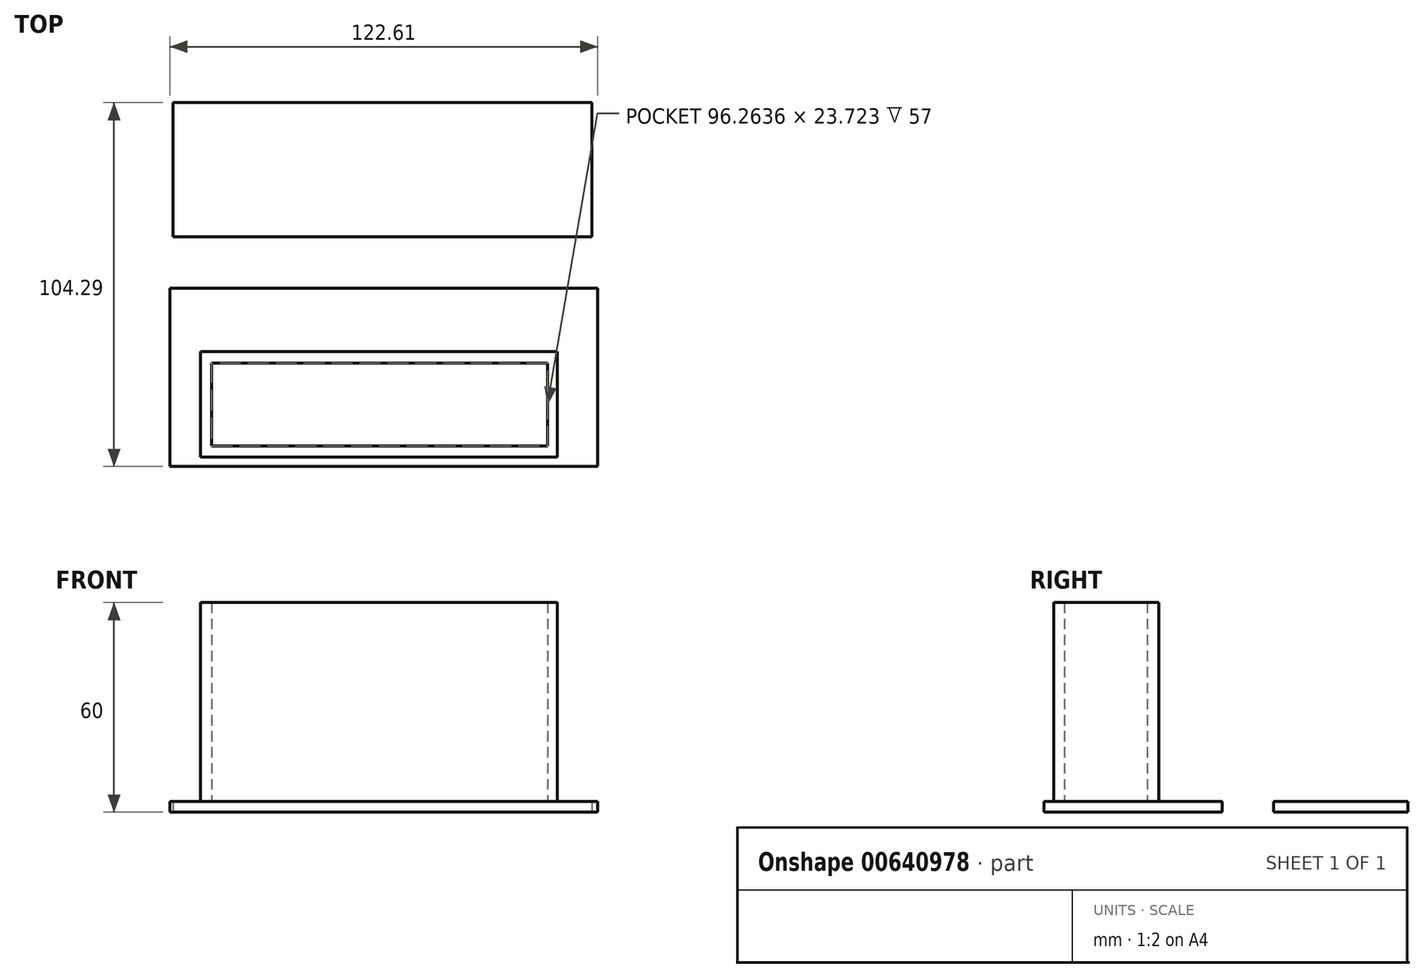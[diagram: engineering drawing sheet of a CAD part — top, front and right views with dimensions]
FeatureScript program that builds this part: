
annotation { "Feature Type Name" : "Feature", "Feature Type Description" : "" }
export const myFeature = defineFeature(function(context is Context, id is Id, definition is map)
    precondition{}
    {
        {
            var Q0;
            Q0=qCreatedBy(makeId("Top.planeOp"),FACE);
            var sketch = newSketch(context, id + "F0", { "sketchPlane" : qUnion([Q0])});
            skLineSegment(sketch, "E0.bottom", {"start": v(-59.84, 38.52) * mm, "end": v(60.16, 38.52) * mm});
            skLineSegment(sketch, "E0.top", {"start": v(-59.84, 0) * mm, "end": v(60.16, 0) * mm});
            skLineSegment(sketch, "E0.left", {"start": v(-59.84, 38.52) * mm, "end": v(-59.84, 0) * mm});
            skLineSegment(sketch, "E0.right", {"start": v(60.16, 38.52) * mm, "end": v(60.16, 0) * mm});
            skLineSegment(sketch, "E1.bottom", {"start": v(-60.7, -14.64) * mm, "end": v(61.9, -14.64) * mm});
            skLineSegment(sketch, "E1.top", {"start": v(-60.7, -65.77) * mm, "end": v(61.9, -65.77) * mm});
            skLineSegment(sketch, "E1.left", {"start": v(-60.7, -14.64) * mm, "end": v(-60.7, -65.77) * mm});
            skLineSegment(sketch, "E1.right", {"start": v(61.9, -14.64) * mm, "end": v(61.9, -65.77) * mm});
            skLineSegment(sketch, "E2.bottom", {"start": v(-51.98, -32.86) * mm, "end": v(50.28, -32.86) * mm});
            skLineSegment(sketch, "E2.top", {"start": v(-51.98, -63.02) * mm, "end": v(50.28, -63.02) * mm});
            skLineSegment(sketch, "E2.left", {"start": v(-51.98, -32.86) * mm, "end": v(-51.98, -63.02) * mm});
            skLineSegment(sketch, "E2.right", {"start": v(50.28, -32.86) * mm, "end": v(50.28, -63.02) * mm});
            skLineSegment(sketch, "E3.bottom", {"start": v(-48.77, -36.16) * mm, "end": v(47.49, -36.16) * mm});
            skLineSegment(sketch, "E3.top", {"start": v(-48.77, -59.88) * mm, "end": v(47.49, -59.88) * mm});
            skLineSegment(sketch, "E3.left", {"start": v(-48.77, -36.16) * mm, "end": v(-48.77, -59.88) * mm});
            skLineSegment(sketch, "E3.right", {"start": v(47.49, -36.16) * mm, "end": v(47.49, -59.88) * mm});
            skSolve(sketch);
        }
        {
            var Q0;
            Q0=makeQuery(id+"F0.imprint","IMPRINT",FACE,{"disambiguationData":[TD([[makeQuery(id+"F0.imprint","IMPRINT",EDGE,{"derivedFrom":sQuery(id+"F0.wireOp",EDGE,"E0.bottom")}),-1.0]])]});
            extrude(context, id + "F1", {"entities" : qUnion([Q0]), "depth" : 3 * mm, "offsetDistance" : 25.4 * mm});
        }
        {
            var Q0;
            Q0=makeQuery(id+"F0.imprint","IMPRINT",FACE,{"disambiguationData":[TD([[makeQuery(id+"F0.imprint","IMPRINT",EDGE,{"derivedFrom":sQuery(id+"F0.wireOp",EDGE,"E1.bottom")}),-1.0]])]});
            extrude(context, id + "F2", {"entities" : qUnion([Q0]), "depth" : 3 * mm, "offsetDistance" : 25.4 * mm});
        }
        {
            var Q0;
            Q0=makeQuery(id+"F0.imprint","IMPRINT",FACE,{"disambiguationData":[TD([[makeQuery(id+"F0.imprint","IMPRINT",EDGE,{"derivedFrom":sQuery(id+"F0.wireOp",EDGE,"E2.bottom")}),-1.0]])]});
            extrude(context, id + "F3", {"entities" : qUnion([Q0]), "operationType" : NewBodyOperationType.ADD, "depth" : 60 * mm, "offsetDistance" : 25.4 * mm});
        }
        {
            var Q0;
            Q0=makeQuery(id+"F0.imprint","IMPRINT",FACE,{"disambiguationData":[TD([[makeQuery(id+"F0.imprint","IMPRINT",EDGE,{"derivedFrom":sQuery(id+"F0.wireOp",EDGE,"E3.bottom")}),-1.0]])]});
            extrude(context, id + "F4", {"entities" : qUnion([Q0]), "operationType" : NewBodyOperationType.ADD, "depth" : 3 * mm, "offsetDistance" : 25.4 * mm});
        }
    });
